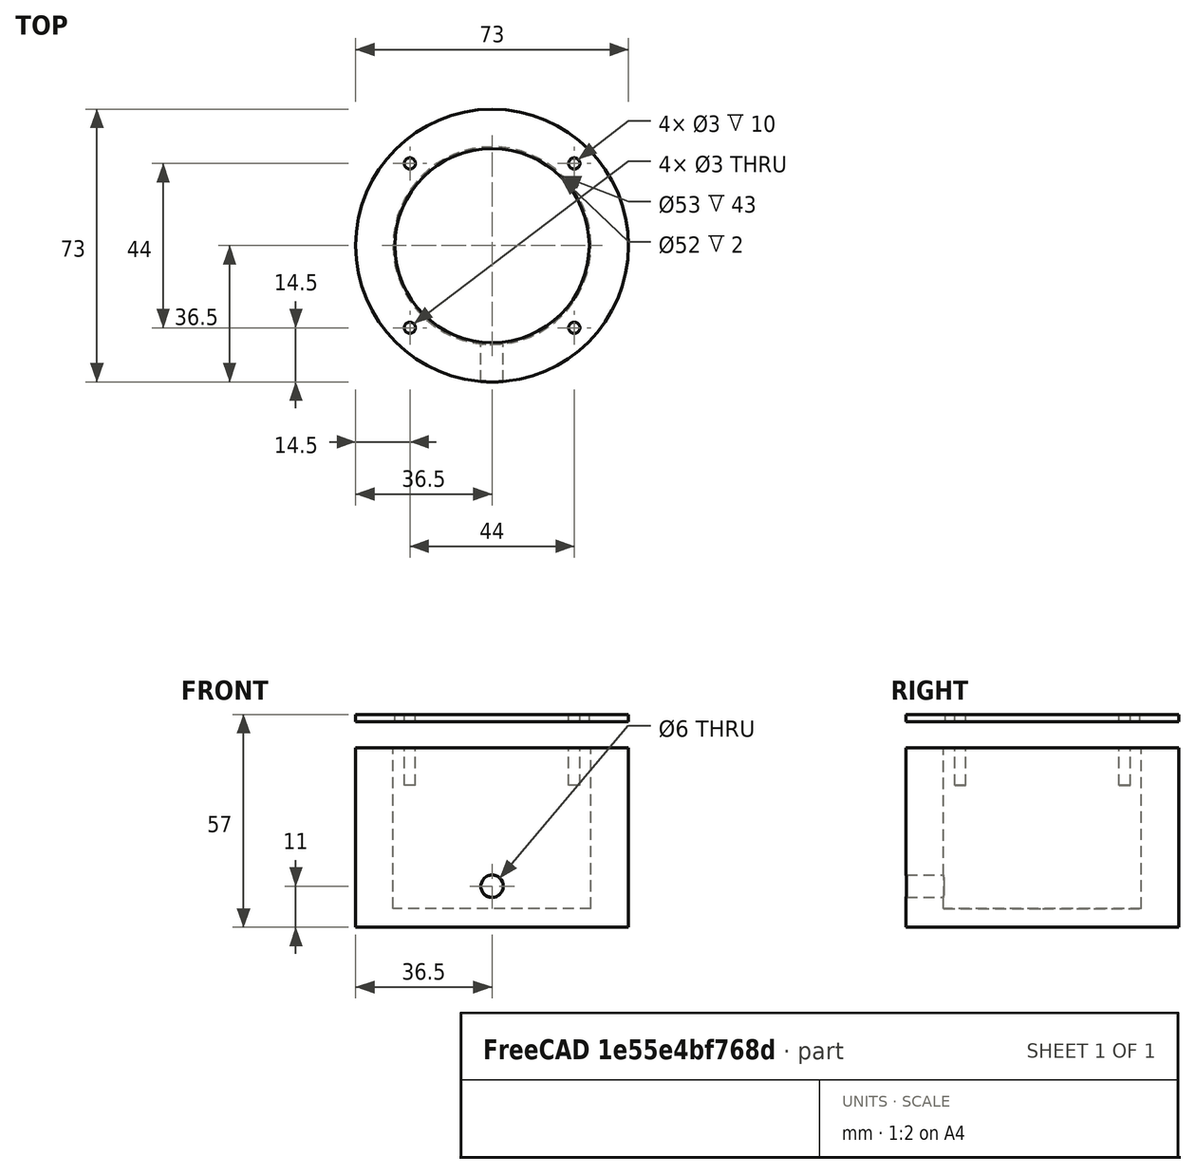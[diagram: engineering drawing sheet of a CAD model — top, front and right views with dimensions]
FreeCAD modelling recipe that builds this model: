
FCSTD DOCUMENT  (FreeCAD 0.17R13522 (Git))
Label: LaBaJia-jwei
License: All rights reserved
LicenseURL: http://en.wikipedia.org/wiki/All_rights_reserved
objects: Part::Cylinder×13, Part::Cut×5, Part::MultiFuse×2
note: 20 computed .brp shape members not serialized (recipe doc carries the construction recipe); baked Part::Feature solids carry a one-line shape summary decoded from their .brp

FEATURE [Part::Cylinder] Cylinder  label="圆柱体"
  Angle = 360
  AttacherType = Attacher::AttachEngine3D
  Height = 45
  Placement = pos=(20,20,20) rot=(0,0,1;0rad)
  Radius = 26.5
FEATURE [Part::Cylinder] Cylinder001  label="圆柱体001"
  Angle = 360
  AttacherType = Attacher::AttachEngine3D
  Height = 48
  Placement = pos=(20,20,15) rot=(0,0,1;0rad)
  Radius = 36.5
FEATURE [Part::Cut] Cut
  Base = -> Cylinder001
  Tool = -> Cylinder
FEATURE [Part::Cylinder] Cylinder002  label="圆柱体002"
  Angle = 360
  AttacherType = Attacher::AttachEngine3D
  Height = 10
  Placement = pos=(42,42,63) rot=(0,0,1;0rad)
  Radius = 1.5
FEATURE [Part::Cylinder] Cylinder003  label="圆柱体003"
  Angle = 360
  AttacherType = Attacher::AttachEngine3D
  Height = 10
  Placement = pos=(-2,42,63) rot=(0,0,1;0rad)
  Radius = 1.5
FEATURE [Part::Cylinder] Cylinder004  label="圆柱体004"
  Angle = 360
  AttacherType = Attacher::AttachEngine3D
  Height = 10
  Placement = pos=(-2,-2,63) rot=(0,0,1;0rad)
  Radius = 1.5
FEATURE [Part::Cylinder] Cylinder005  label="圆柱体005"
  Angle = 360
  AttacherType = Attacher::AttachEngine3D
  Height = 10
  Placement = pos=(42,-2,63) rot=(0,0,1;0rad)
  Radius = 1.5
FEATURE [Part::MultiFuse] Fusion
  Placement = pos=(0,0,-10) rot=(0,0,1;0rad)
  Shapes = -> [Cylinder005,Cylinder004,Cylinder002,Cylinder003]
FEATURE [Part::Cut] Cut001
  Base = -> Cut
  Tool = -> Fusion
FEATURE [Part::Cylinder] Cylinder006  label="圆柱体006"
  Angle = 360
  AttacherType = Attacher::AttachEngine3D
  Height = 2
  Placement = pos=(20,20,20) rot=(0,0,1;0rad)
  Radius = 36.5
FEATURE [Part::Cylinder] Cylinder007  label="圆柱体007"
  Angle = 360
  AttacherType = Attacher::AttachEngine3D
  Height = 2
  Placement = pos=(20,20,20) rot=(0,0,1;0rad)
  Radius = 26
FEATURE [Part::Cylinder] Cylinder008  label="圆柱体008"
  Angle = 360
  AttacherType = Attacher::AttachEngine3D
  Height = 10
  Placement = pos=(42,42,63) rot=(0,0,1;0rad)
  Radius = 1.5
FEATURE [Part::Cylinder] Cylinder009  label="圆柱体009"
  Angle = 360
  AttacherType = Attacher::AttachEngine3D
  Height = 10
  Placement = pos=(-2,42,63) rot=(0,0,1;0rad)
  Radius = 1.5
FEATURE [Part::Cylinder] Cylinder010  label="圆柱体010"
  Angle = 360
  AttacherType = Attacher::AttachEngine3D
  Height = 10
  Placement = pos=(-2,-2,63) rot=(0,0,1;0rad)
  Radius = 1.5
FEATURE [Part::Cylinder] Cylinder011  label="圆柱体011"
  Angle = 360
  AttacherType = Attacher::AttachEngine3D
  Height = 10
  Placement = pos=(42,-2,63) rot=(0,0,1;0rad)
  Radius = 1.5
FEATURE [Part::MultiFuse] Fusion001
  Shapes = -> [Cylinder011,Cylinder010,Cylinder008,Cylinder009]
FEATURE [Part::Cut] Cut002
  Base = -> Cylinder006
  Placement = pos=(0,0,50) rot=(0,0,1;0rad)
  Tool = -> Cylinder007
FEATURE [Part::Cut] Cut003
  Base = -> Cut002
  Tool = -> Fusion001
FEATURE [Part::Cylinder] Cylinder012  label="圆柱体012"
  Angle = 360
  AttacherType = Attacher::AttachEngine3D
  Height = 20
  Placement = pos=(20,-20,26) rot=(1,0,0;4.71239rad)
  Radius = 3
FEATURE [Part::Cut] Cut004
  Base = -> Cut001
  Tool = -> Cylinder012
